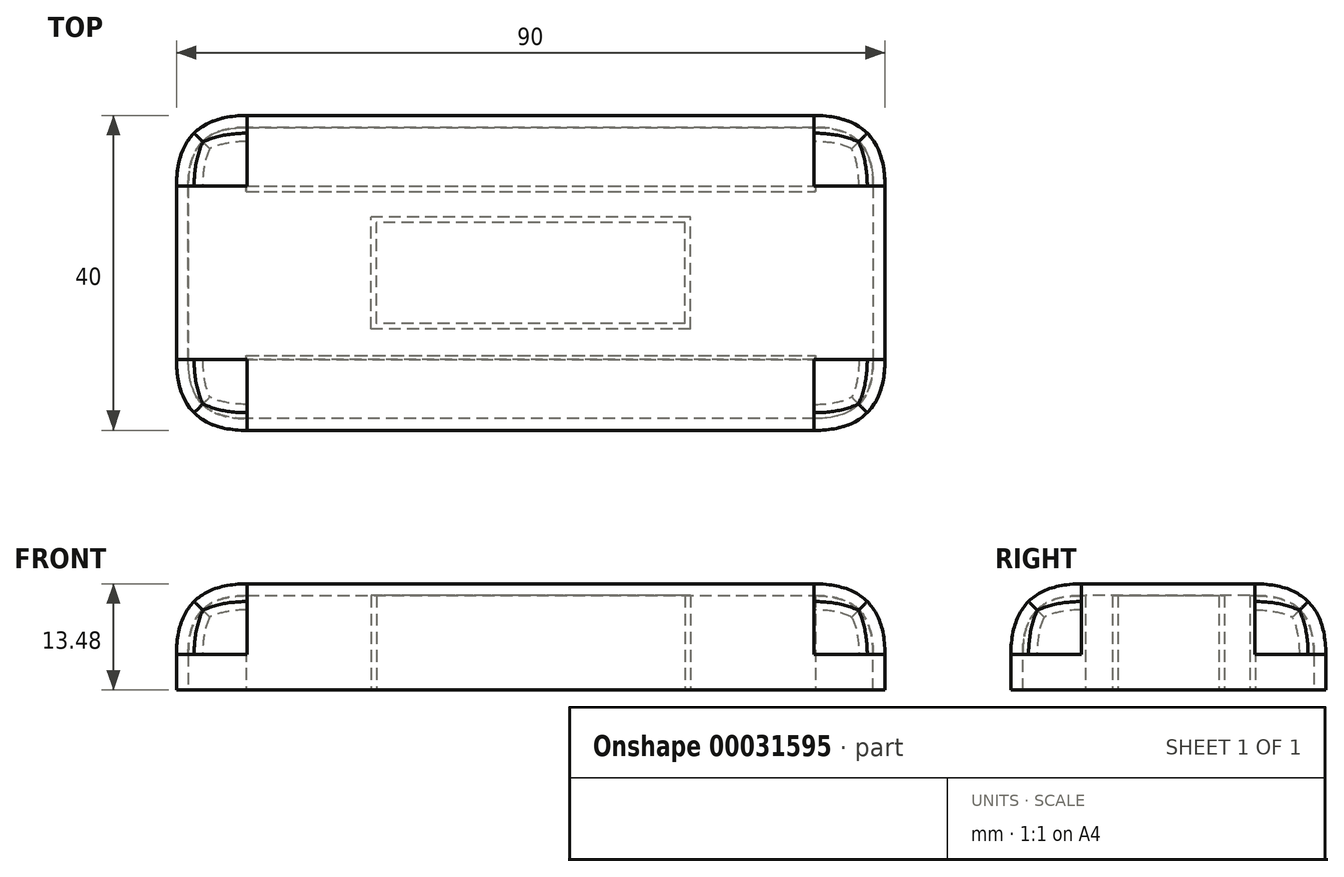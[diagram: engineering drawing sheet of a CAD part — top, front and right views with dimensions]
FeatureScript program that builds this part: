
annotation { "Feature Type Name" : "Feature", "Feature Type Description" : "" }
export const myFeature = defineFeature(function(context is Context, id is Id, definition is map)
    precondition{}
    {
        {
            var Q0;
            Q0=qCreatedBy(makeId("Top.planeOp"),FACE);
            var sketch = newSketch(context, id + "F0", { "sketchPlane" : qUnion([Q0])});
            skLineSegment(sketch, "E0.rect.bottom", {"start": v(45, 20) * mm, "end": v(-45, 20) * mm});
            skLineSegment(sketch, "E0.rect.top", {"start": v(45, -20) * mm, "end": v(-45, -20) * mm});
            skLineSegment(sketch, "E0.rect.left", {"start": v(45, 20) * mm, "end": v(45, -20) * mm});
            skLineSegment(sketch, "E0.rect.right", {"start": v(-45, 20) * mm, "end": v(-45, -20) * mm});
            skPoint(sketch, "E0.rect.middle", {"position": v(0, 0) * mm});
            skSolve(sketch);
        }
        {
            var Q0;
            Q0=makeQuery(id+"F0.imprint","IMPRINT",FACE,{"disambiguationData":[TD([[makeQuery(id+"F0.imprint","IMPRINT",EDGE,{"derivedFrom":sQuery(id+"F0.wireOp",EDGE,"E0.rect.bottom")}),1.0]])]});
            extrude(context, id + "F1", {"entities" : qUnion([Q0]), "depth" : 13.48 * mm});
        }
        {
            var Q0;
            Q0=makeQuery(id+"F1.opExtrude","CAP_EDGE",EDGE,{"disambiguationData":[OSD([sQuery(id+"F0.wireOp",EDGE,"E0.rect.right")])],"isStart":false});
            var Q1;
            Q1=makeQuery(id+"F1.opExtrude","CAP_EDGE",EDGE,{"disambiguationData":[OSD([sQuery(id+"F0.wireOp",EDGE,"E0.rect.bottom")])],"isStart":false});
            var Q2;
            Q2=makeQuery(id+"F1.opExtrude","CAP_EDGE",EDGE,{"disambiguationData":[OSD([sQuery(id+"F0.wireOp",EDGE,"E0.rect.left")])],"isStart":false});
            var Q3;
            Q3=makeQuery(id+"F1.opExtrude","SWEPT_EDGE",EDGE,{"disambiguationData":[OSD([sQuery(id+"F0.wireOp",EDGE,"E0.rect.top"),sQuery(id+"F0.wireOp",EDGE,"E0.rect.right")])]});
            var Q4;
            Q4=makeQuery(id+"F1.opExtrude","CAP_EDGE",EDGE,{"disambiguationData":[OSD([sQuery(id+"F0.wireOp",EDGE,"E0.rect.top")])],"isStart":false});
            var Q5;
            Q5=makeQuery(id+"F1.opExtrude","SWEPT_EDGE",EDGE,{"disambiguationData":[OSD([sQuery(id+"F0.wireOp",EDGE,"E0.rect.top"),sQuery(id+"F0.wireOp",EDGE,"E0.rect.left")])]});
            var Q6;
            Q6=makeQuery(id+"F1.opExtrude","SWEPT_EDGE",EDGE,{"disambiguationData":[OSD([sQuery(id+"F0.wireOp",EDGE,"E0.rect.bottom"),sQuery(id+"F0.wireOp",EDGE,"E0.rect.left")])]});
            var Q7;
            Q7=makeQuery(id+"F1.opExtrude","SWEPT_EDGE",EDGE,{"disambiguationData":[OSD([sQuery(id+"F0.wireOp",EDGE,"E0.rect.bottom"),sQuery(id+"F0.wireOp",EDGE,"E0.rect.right")])]});
            fillet(context, id + "F2", {"entities" : qUnion([Q0, Q1, Q2, Q3, Q4, Q5, Q6, Q7]), "radius" : 8.98 * mm, "tangentPropagation" : true, "rho" : 0.5, "crossSection" : FilletCrossSection.CONIC, "allowEdgeOverflow" : false});
        }
        {
            var Q0;
            Q0=makeQuery(id+"F1.opExtrude","CAP_FACE",FACE,{"disambiguationData":[OSD([sQuery(id+"F0.wireOp",EDGE,"E0.rect.bottom"),sQuery(id+"F0.wireOp",EDGE,"E0.rect.top"),sQuery(id+"F0.wireOp",EDGE,"E0.rect.left"),sQuery(id+"F0.wireOp",EDGE,"E0.rect.right")])],"isStart":true});
            var Q1;
            Q1=makeQuery(id+"F1.opExtrude","SWEPT_BODY",BODY,{"disambiguationData":[OSD([sQuery(id+"F0.wireOp",EDGE,"E0.rect.bottom"),sQuery(id+"F0.wireOp",EDGE,"E0.rect.top"),sQuery(id+"F0.wireOp",EDGE,"E0.rect.left"),sQuery(id+"F0.wireOp",EDGE,"E0.rect.right")])]});
            shell(context, id + "F3", {"entities" : qUnion([Q0]), "parts" : qUnion([Q1]), "thickness" : 1.5 * mm});
        }
        {
            var Q0;
            Q0=makeQuery(id+"F1.opExtrude","CAP_FACE",FACE,{"disambiguationData":[OSD([sQuery(id+"F0.wireOp",EDGE,"E0.rect.bottom"),sQuery(id+"F0.wireOp",EDGE,"E0.rect.top"),sQuery(id+"F0.wireOp",EDGE,"E0.rect.left"),sQuery(id+"F0.wireOp",EDGE,"E0.rect.right")])],"isStart":true});
            var sketch = newSketch(context, id + "F4", { "sketchPlane" : qUnion([Q0])});
            skLineSegment(sketch, "E1.rect.bottom", {"start": v(20.3, 7.11) * mm, "end": v(-20.3, 7.11) * mm});
            skLineSegment(sketch, "E1.rect.top", {"start": v(20.3, -7.11) * mm, "end": v(-20.3, -7.11) * mm});
            skLineSegment(sketch, "E1.rect.left", {"start": v(20.3, 7.11) * mm, "end": v(20.3, -7.11) * mm});
            skLineSegment(sketch, "E1.rect.right", {"start": v(-20.3, 7.11) * mm, "end": v(-20.3, -7.11) * mm});
            skPoint(sketch, "E1.rect.middle", {"position": v(0, 0) * mm});
            skLineSegment(sketch, "E2", {"start": v(-36.16, 11) * mm, "end": v(36.2, 11) * mm});
            skLineSegment(sketch, "E3", {"start": v(-36.16, -11.06) * mm, "end": v(36.2, -11.06) * mm});
            skLineSegment(sketch, "E4.0", {"start": v(-36.16, 10.52) * mm, "end": v(36.2, 10.52) * mm});
            skLineSegment(sketch, "E5", {"start": v(-36.16, 10.52) * mm, "end": v(-36.16, 11) * mm});
            skLineSegment(sketch, "E6", {"start": v(36.2, 11) * mm, "end": v(36.2, 10.52) * mm});
            skLineSegment(sketch, "E7.0", {"start": v(19.6, 6.41) * mm, "end": v(-19.6, 6.41) * mm});
            skLineSegment(sketch, "E7.1", {"start": v(19.6, 6.41) * mm, "end": v(19.6, -6.41) * mm});
            skLineSegment(sketch, "E7.2", {"start": v(19.6, -6.41) * mm, "end": v(-19.6, -6.41) * mm});
            skLineSegment(sketch, "E7.3", {"start": v(-19.6, 6.41) * mm, "end": v(-19.6, -6.41) * mm});
            skLineSegment(sketch, "E8.0", {"start": v(-36.16, -10.33) * mm, "end": v(36.2, -10.33) * mm});
            skLineSegment(sketch, "E9", {"start": v(36.2, -11.06) * mm, "end": v(36.2, -10.33) * mm});
            skLineSegment(sketch, "E10", {"start": v(-36.16, -11.06) * mm, "end": v(-36.16, -10.33) * mm});
            skSolve(sketch);
        }
        {
            var Q0;
            Q0 = qSketchRegion(id + "F4", true);
            var Q1;
            Q1=makeQuery(id+"F3.opShell","OFFSET_FACE",FACE,{"disambiguationData":[OSD([sQuery(id+"F0.wireOp",EDGE,"E0.rect.bottom"),sQuery(id+"F0.wireOp",EDGE,"E0.rect.top"),sQuery(id+"F0.wireOp",EDGE,"E0.rect.left"),sQuery(id+"F0.wireOp",EDGE,"E0.rect.right")])]});
            extrude(context, id + "F5", {"entities" : qUnion([Q0]), "operationType" : NewBodyOperationType.ADD, "endBound" : BoundingType.UP_TO_SURFACE, "oppositeDirection" : true, "endBoundEntityFace" : qUnion([Q1]), "depth" : 26.32 * mm});
        }
    });
